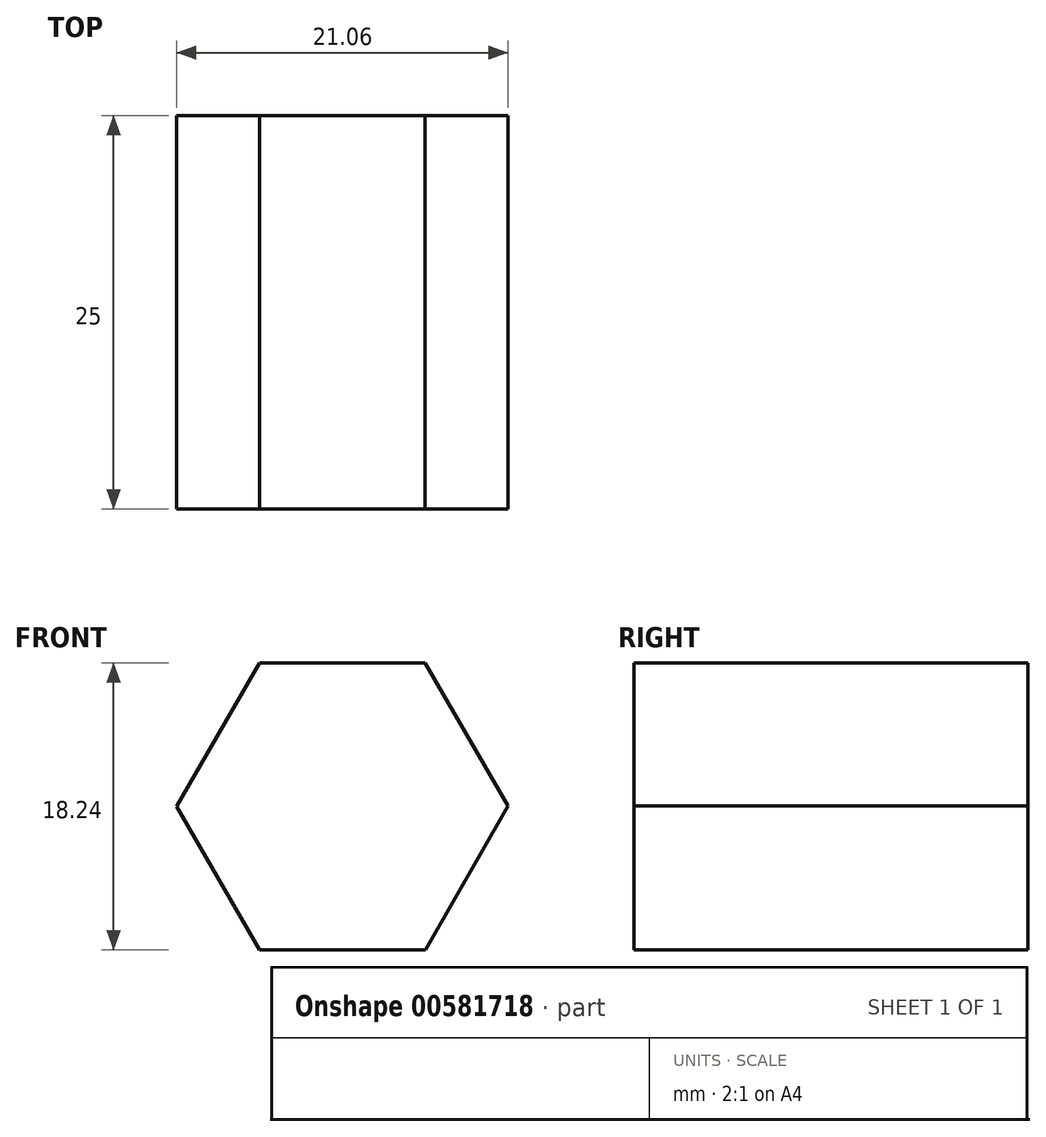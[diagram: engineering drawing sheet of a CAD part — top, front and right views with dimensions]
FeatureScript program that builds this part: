
annotation { "Feature Type Name" : "Feature", "Feature Type Description" : "" }
export const myFeature = defineFeature(function(context is Context, id is Id, definition is map)
    precondition{}
    {
        {
            var Q0;
            Q0=qCreatedBy(makeId("Front.planeOp"),FACE);
            var sketch = newSketch(context, id + "F0", { "sketchPlane" : qUnion([Q0])});
            skCircle(sketch, "E0.cCircle", {"center": v(0, 0) * mm, "radius": 9.11 * mm, "construction": true});
            skLineSegment(sketch, "E0.0", {"start": v(10.53, 0.01) * mm, "end": v(5.27, -9.1) * mm});
            skLineSegment(sketch, "E0.1", {"start": v(5.27, -9.1) * mm, "end": v(-5.25, -9.12) * mm});
            skLineSegment(sketch, "E0.2", {"start": v(-5.25, -9.12) * mm, "end": v(-10.53, -0.01) * mm});
            skLineSegment(sketch, "E0.3", {"start": v(-10.53, -0.01) * mm, "end": v(-5.27, 9.1) * mm});
            skLineSegment(sketch, "E0.4", {"start": v(-5.27, 9.1) * mm, "end": v(5.25, 9.12) * mm});
            skLineSegment(sketch, "E0.5", {"start": v(5.25, 9.12) * mm, "end": v(10.53, 0.01) * mm});
            skPoint(sketch, "E0.0.midPoint", {"position": v(7.9, -4.55) * mm});
            skSolve(sketch);
        }
        {
            var Q0;
            Q0=makeQuery(id+"F0.imprint","IMPRINT",FACE,{"disambiguationData":[TD([[makeQuery(id+"F0.imprint","IMPRINT",EDGE,{"derivedFrom":sQuery(id+"F0.wireOp",EDGE,"E0.0")}),-1.0]])]});
            extrude(context, id + "F1", {"entities" : qUnion([Q0]), "depth" : 25 * mm, "offsetDistance" : 25 * mm});
        }
    });
